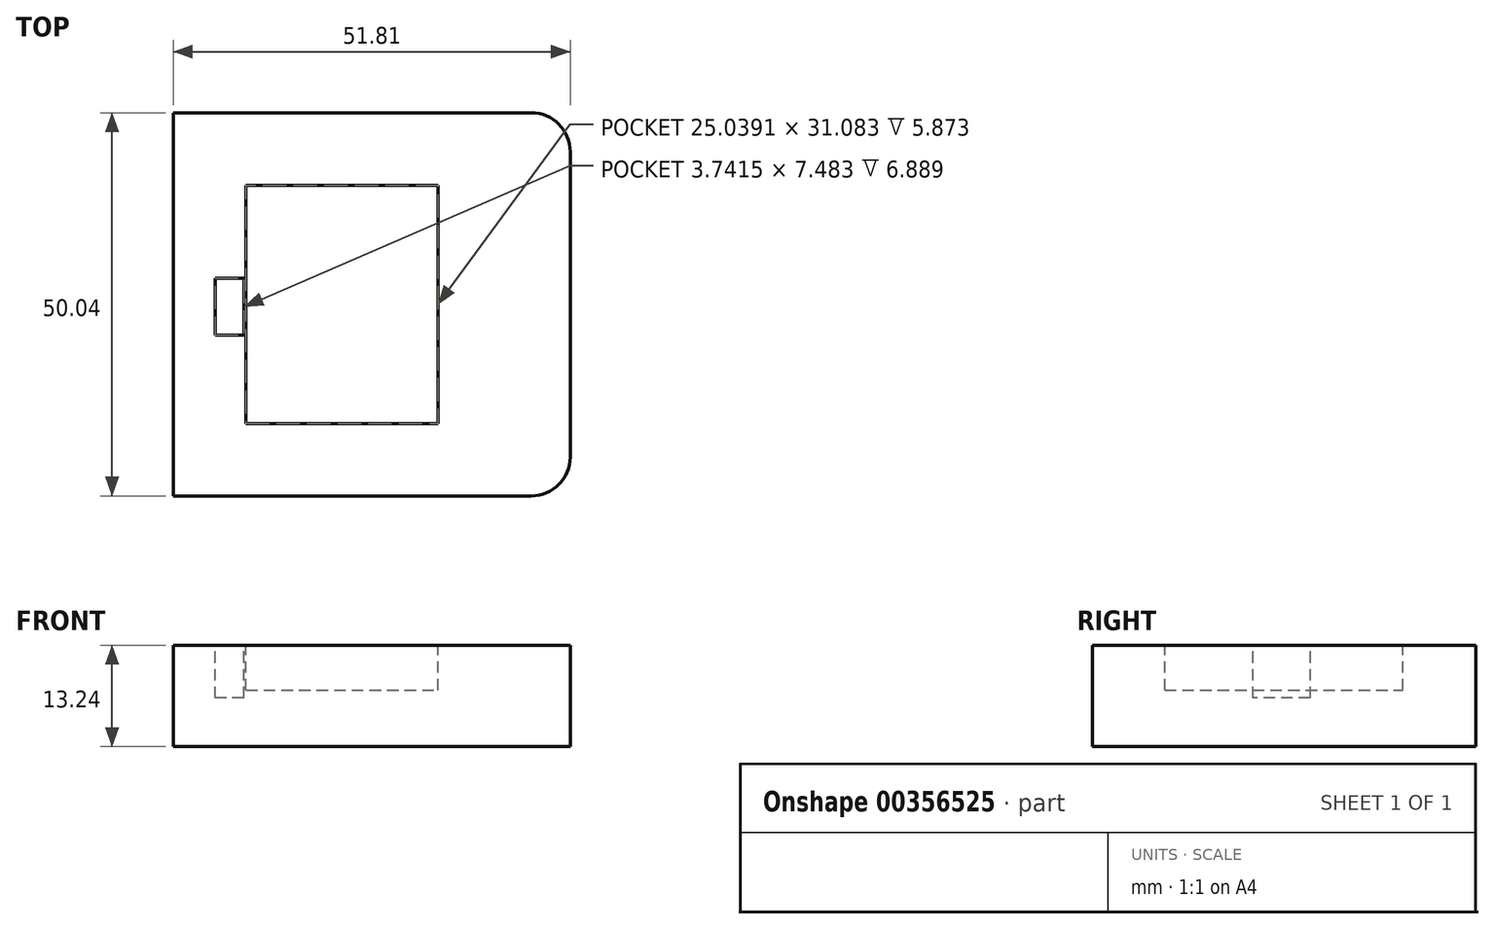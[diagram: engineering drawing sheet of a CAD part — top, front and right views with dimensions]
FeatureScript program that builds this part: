
annotation { "Feature Type Name" : "Feature", "Feature Type Description" : "" }
export const myFeature = defineFeature(function(context is Context, id is Id, definition is map)
    precondition{}
    {
        {
            var Q0;
            Q0=qCreatedBy(makeId("Front.planeOp"),FACE);
            var sketch = newSketch(context, id + "F0", { "sketchPlane" : qUnion([Q0])});
            skLineSegment(sketch, "E0.bottom", {"start": v(0, 0) * mm, "end": v(51.8, 0) * mm});
            skLineSegment(sketch, "E0.top", {"start": v(0, 13.24) * mm, "end": v(51.8, 13.24) * mm});
            skLineSegment(sketch, "E0.left", {"start": v(0, 0) * mm, "end": v(0, 13.24) * mm});
            skLineSegment(sketch, "E0.right", {"start": v(51.8, 0) * mm, "end": v(51.8, 13.24) * mm});
            skSolve(sketch);
        }
        {
            var Q0;
            Q0 = qSketchRegion(id + "F0", true);
            extrude(context, id + "F1", {"entities" : qUnion([Q0]), "depth" : 50.04 * mm});
        }
        {
            var Q0;
            Q0=makeQuery(id+"F1.opExtrude","CAP_EDGE",EDGE,{"disambiguationData":[OSD([sQuery(id+"F0.wireOp",EDGE,"E0.right")])],"isStart":false});
            fillet(context, id + "F2", {"entities" : qUnion([Q0]), "radius" : 5.08 * mm, "tangentPropagation" : true, "allowEdgeOverflow" : false});
        }
        {
            var Q0;
            Q0=makeQuery(id+"F1.opExtrude","CAP_EDGE",EDGE,{"disambiguationData":[OSD([sQuery(id+"F0.wireOp",EDGE,"E0.right")])],"isStart":true});
            fillet(context, id + "F3", {"entities" : qUnion([Q0]), "radius" : 5.08 * mm, "tangentPropagation" : true, "allowEdgeOverflow" : false});
        }
        {
            var Q0;
            Q0=qCreatedBy(makeId("Top.planeOp"),FACE);
            var sketch = newSketch(context, id + "F4", { "sketchPlane" : qUnion([Q0])});
            skLineSegment(sketch, "E1.bottom", {"start": v(9.5, -40.58) * mm, "end": v(34.54, -40.58) * mm});
            skLineSegment(sketch, "E1.top", {"start": v(9.5, -9.5) * mm, "end": v(34.54, -9.5) * mm});
            skLineSegment(sketch, "E1.left", {"start": v(9.5, -40.58) * mm, "end": v(9.5, -9.5) * mm});
            skLineSegment(sketch, "E1.right", {"start": v(34.54, -40.58) * mm, "end": v(34.54, -9.5) * mm});
            skSolve(sketch);
        }
        {
            var Q0;
            Q0=makeQuery(id+"F4.imprint","IMPRINT",FACE,{"disambiguationData":[TD([[makeQuery(id+"F4.imprint","IMPRINT",EDGE,{"derivedFrom":sQuery(id+"F4.wireOp",EDGE,"E1.bottom")}),1.0]])]});
            extrude(context, id + "F5", {"entities" : qUnion([Q0]), "operationType" : NewBodyOperationType.ADD, "depth" : 38.35 * mm});
        }
        {
            var Q0;
            Q0=makeQuery(id+"F5.opExtrude","CAP_FACE",FACE,{"disambiguationData":[OSD([sQuery(id+"F4.wireOp",EDGE,"E1.bottom"),sQuery(id+"F4.wireOp",EDGE,"E1.top"),sQuery(id+"F4.wireOp",EDGE,"E1.left"),sQuery(id+"F4.wireOp",EDGE,"E1.right")])],"isStart":false});
            extrude(context, id + "F6", {"entities" : qUnion([Q0]), "operationType" : NewBodyOperationType.REMOVE, "oppositeDirection" : true, "depth" : 30.99 * mm});
        }
        {
            var Q0;
            Q0=qCreatedBy(makeId("Top.planeOp"),FACE);
            var sketch = newSketch(context, id + "F7", { "sketchPlane" : qUnion([Q0])});
            skLineSegment(sketch, "E2.bottom", {"start": v(9.2, -21.59) * mm, "end": v(5.47, -21.59) * mm});
            skLineSegment(sketch, "E2.top", {"start": v(9.2, -29.07) * mm, "end": v(5.47, -29.07) * mm});
            skLineSegment(sketch, "E2.left", {"start": v(9.2, -21.59) * mm, "end": v(9.2, -29.07) * mm});
            skLineSegment(sketch, "E2.right", {"start": v(5.47, -21.59) * mm, "end": v(5.47, -29.07) * mm});
            skSolve(sketch);
        }
        {
            var Q0;
            Q0=makeQuery(id+"F7.imprint","IMPRINT",FACE,{"disambiguationData":[TD([[makeQuery(id+"F7.imprint","IMPRINT",EDGE,{"derivedFrom":sQuery(id+"F7.wireOp",EDGE,"E2.bottom")}),1.0]])]});
            extrude(context, id + "F8", {"entities" : qUnion([Q0]), "operationType" : NewBodyOperationType.ADD, "depth" : 33.27 * mm});
        }
        {
            var Q0;
            Q0=makeQuery(id+"F8.opExtrude","CAP_FACE",FACE,{"disambiguationData":[OSD([sQuery(id+"F7.wireOp",EDGE,"E2.bottom"),sQuery(id+"F7.wireOp",EDGE,"E2.top"),sQuery(id+"F7.wireOp",EDGE,"E2.left"),sQuery(id+"F7.wireOp",EDGE,"E2.right")])],"isStart":false});
            extrude(context, id + "F9", {"entities" : qUnion([Q0]), "operationType" : NewBodyOperationType.REMOVE, "oppositeDirection" : true, "depth" : 26.92 * mm});
        }
    });
